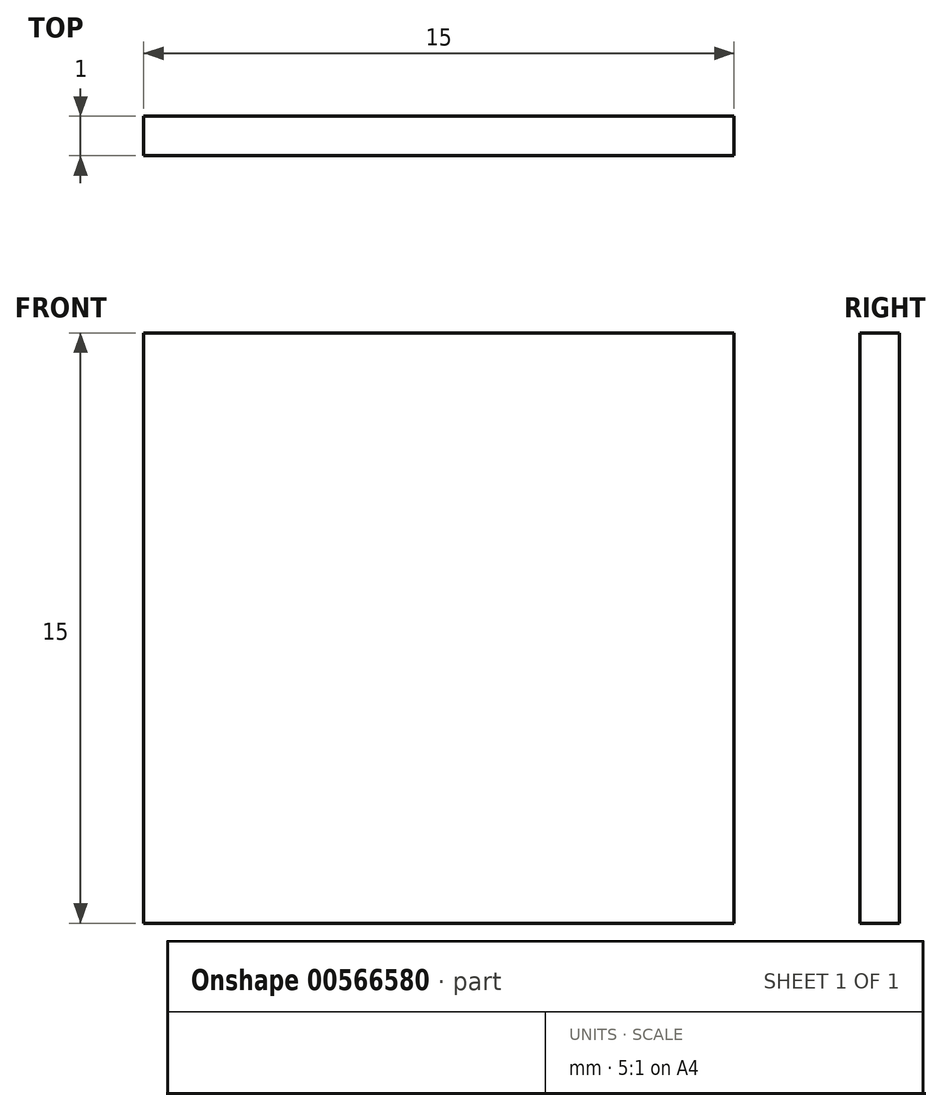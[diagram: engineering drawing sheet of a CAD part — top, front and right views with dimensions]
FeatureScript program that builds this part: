
annotation { "Feature Type Name" : "Feature", "Feature Type Description" : "" }
export const myFeature = defineFeature(function(context is Context, id is Id, definition is map)
    precondition{}
    {
        {
            var Q0;
            Q0=qCreatedBy(makeId("Front.planeOp"),FACE);
            var sketch = newSketch(context, id + "F0", { "sketchPlane" : qUnion([Q0])});
            skLineSegment(sketch, "E0", {"start": v(-45.04, -13.61) * mm, "end": v(-45.04, -28.61) * mm});
            skLineSegment(sketch, "E1", {"start": v(-45.04, -28.61) * mm, "end": v(-30.04, -28.61) * mm});
            skLineSegment(sketch, "E2", {"start": v(-30.04, -28.61) * mm, "end": v(-30.04, -13.61) * mm});
            skLineSegment(sketch, "E3", {"start": v(-30.04, -13.61) * mm, "end": v(-45.04, -13.61) * mm});
            skSolve(sketch);
        }
        {
            var Q0;
            Q0=makeQuery(id+"F0.imprint","IMPRINT",FACE,{"disambiguationData":[TD([[makeQuery(id+"F0.imprint","IMPRINT",EDGE,{"derivedFrom":sQuery(id+"F0.wireOp",EDGE,"E0")}),1.0]])]});
            extrude(context, id + "F1", {"entities" : qUnion([Q0]), "depth" : 1 * mm, "offsetDistance" : 25 * mm});
        }
    });
